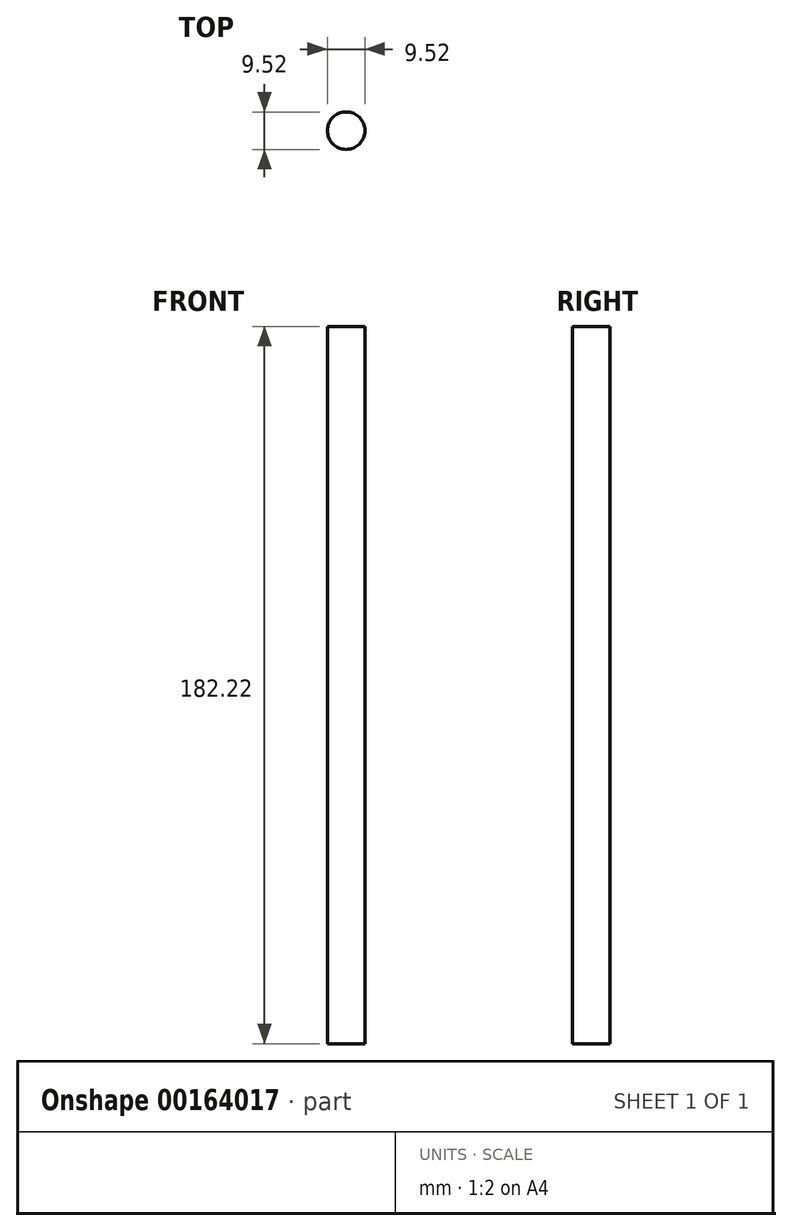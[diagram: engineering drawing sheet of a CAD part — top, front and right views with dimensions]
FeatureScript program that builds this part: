
annotation { "Feature Type Name" : "Feature", "Feature Type Description" : "" }
export const myFeature = defineFeature(function(context is Context, id is Id, definition is map)
    precondition{}
    {
        {
            var Q0;
            Q0=qCreatedBy(makeId("Top.planeOp"),FACE);
            var sketch = newSketch(context, id + "F0", { "sketchPlane" : qUnion([Q0])});
            skCircle(sketch, "E0", {"center": v(0, 0) * mm, "radius": 4.76 * mm});
            skSolve(sketch);
        }
        {
            var Q0;
            Q0=makeQuery(id+"F0.imprint","IMPRINT",FACE,{"disambiguationData":[TD([[makeQuery(id+"F0.imprint","IMPRINT",EDGE,{"derivedFrom":sQuery(id+"F0.wireOp",EDGE,"E0")}),1.0]])]});
            extrude(context, id + "F1", {"entities" : qUnion([Q0]), "depth" : 182.22 * mm});
        }
    });
